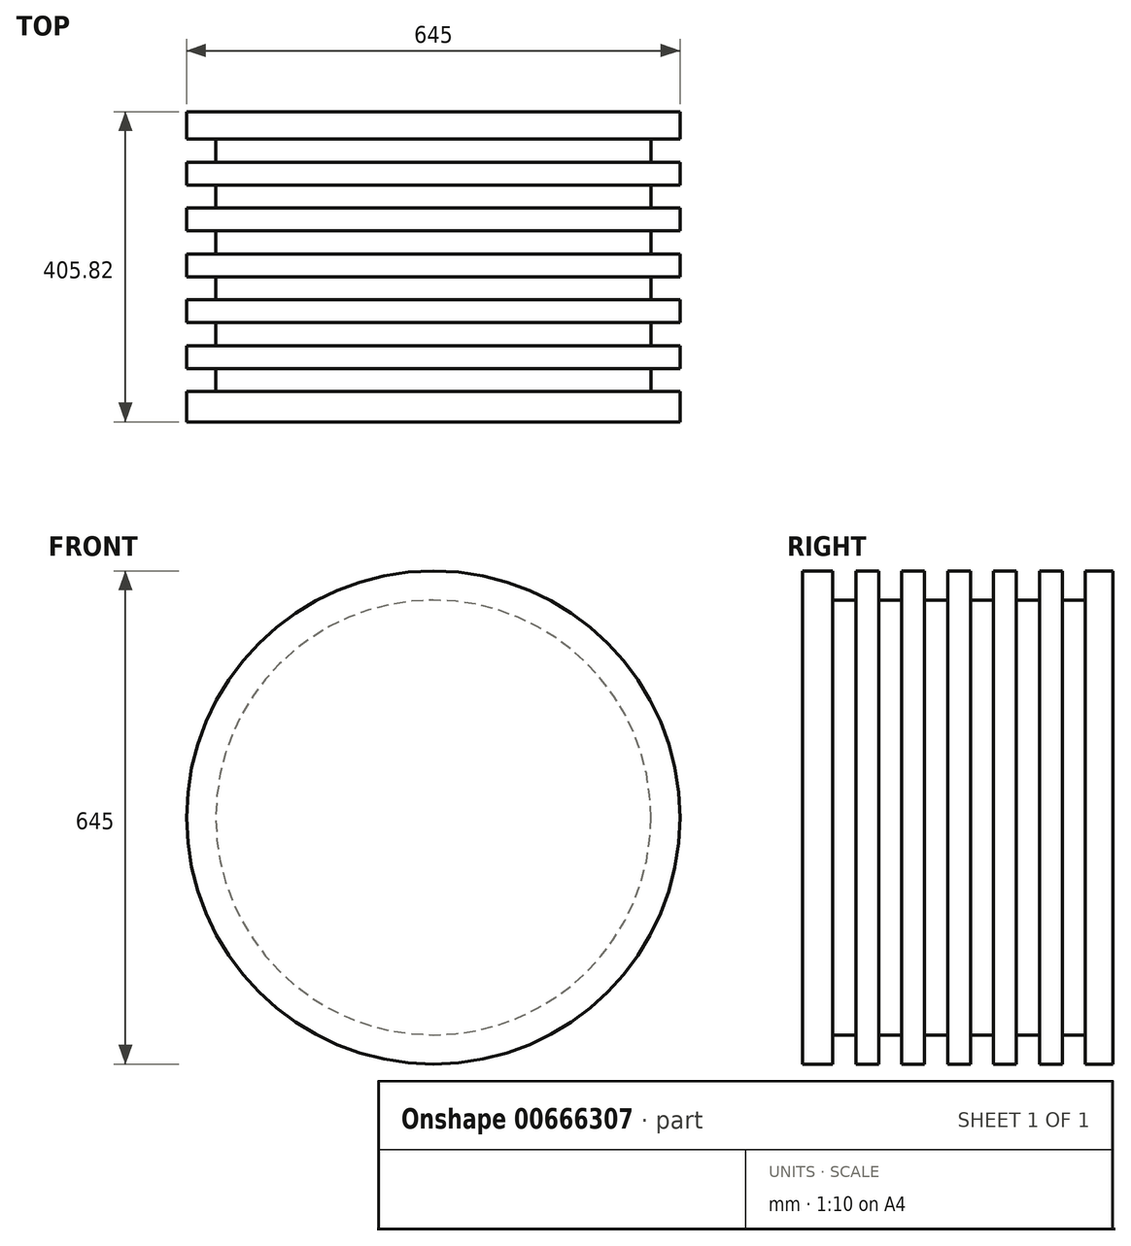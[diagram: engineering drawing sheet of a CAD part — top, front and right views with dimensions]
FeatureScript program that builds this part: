
annotation { "Feature Type Name" : "Feature", "Feature Type Description" : "" }
export const myFeature = defineFeature(function(context is Context, id is Id, definition is map)
    precondition{}
    {
        {
            var Q0;
            Q0=qCreatedBy(makeId("Front.planeOp"),FACE);
            var sketch = newSketch(context, id + "F0", { "sketchPlane" : qUnion([Q0])});
            skCircle(sketch, "E0", {"center": v(0, 0) * mm, "radius": 322.5 * mm});
            skSolve(sketch);
        }
        {
            var Q0;
            Q0=qSketchRegion(id+"F0",true);
            extrude(context, id + "F1", {"entities" : qUnion([Q0]), "depth" : 405.82 * mm});
        }
        {
            var Q0;
            Q0=qCreatedBy(makeId("Right.planeOp"),FACE);
            var sketch = newSketch(context, id + "F2", { "sketchPlane" : qUnion([Q0])});
            skLineSegment(sketch, "E1.bottom", {"start": v(-366.07, 340.51) * mm, "end": v(-336.07, 340.51) * mm});
            skLineSegment(sketch, "E1.top", {"start": v(-366.07, 284.36) * mm, "end": v(-336.07, 284.36) * mm});
            skLineSegment(sketch, "E1.left", {"start": v(-366.07, 340.51) * mm, "end": v(-366.07, 284.36) * mm});
            skLineSegment(sketch, "E1.right", {"start": v(-336.07, 340.51) * mm, "end": v(-336.07, 284.36) * mm});
            skLineSegment(sketch, "E2.1.0.0", {"start": v(-276.07, 340.51) * mm, "end": v(-276.07, 284.36) * mm});
            skLineSegment(sketch, "E2.1.0.1", {"start": v(-306.07, 340.51) * mm, "end": v(-306.07, 284.36) * mm});
            skLineSegment(sketch, "E2.1.0.2", {"start": v(-306.07, 284.36) * mm, "end": v(-276.07, 284.36) * mm});
            skLineSegment(sketch, "E2.1.0.3", {"start": v(-306.07, 340.51) * mm, "end": v(-276.07, 340.51) * mm});
            skLineSegment(sketch, "E2.2.0.0", {"start": v(-216.07, 340.51) * mm, "end": v(-216.07, 284.36) * mm});
            skLineSegment(sketch, "E2.2.0.1", {"start": v(-246.07, 340.51) * mm, "end": v(-246.07, 284.36) * mm});
            skLineSegment(sketch, "E2.2.0.2", {"start": v(-246.07, 284.36) * mm, "end": v(-216.07, 284.36) * mm});
            skLineSegment(sketch, "E2.2.0.3", {"start": v(-246.07, 340.51) * mm, "end": v(-216.07, 340.51) * mm});
            skLineSegment(sketch, "E2.3.0.0", {"start": v(-156.07, 340.51) * mm, "end": v(-156.07, 284.36) * mm});
            skLineSegment(sketch, "E2.3.0.1", {"start": v(-186.07, 340.51) * mm, "end": v(-186.07, 284.36) * mm});
            skLineSegment(sketch, "E2.3.0.2", {"start": v(-186.07, 284.36) * mm, "end": v(-156.07, 284.36) * mm});
            skLineSegment(sketch, "E2.3.0.3", {"start": v(-186.07, 340.51) * mm, "end": v(-156.07, 340.51) * mm});
            skLineSegment(sketch, "E2.4.0.0", {"start": v(-96.07, 340.51) * mm, "end": v(-96.07, 284.36) * mm});
            skLineSegment(sketch, "E2.4.0.1", {"start": v(-126.07, 340.51) * mm, "end": v(-126.07, 284.36) * mm});
            skLineSegment(sketch, "E2.4.0.2", {"start": v(-126.07, 284.36) * mm, "end": v(-96.07, 284.36) * mm});
            skLineSegment(sketch, "E2.4.0.3", {"start": v(-126.07, 340.51) * mm, "end": v(-96.07, 340.51) * mm});
            skLineSegment(sketch, "E2.5.0.0", {"start": v(-36.07, 340.51) * mm, "end": v(-36.07, 284.36) * mm});
            skLineSegment(sketch, "E2.5.0.1", {"start": v(-66.07, 340.51) * mm, "end": v(-66.07, 284.36) * mm});
            skLineSegment(sketch, "E2.5.0.2", {"start": v(-66.07, 284.36) * mm, "end": v(-36.07, 284.36) * mm});
            skLineSegment(sketch, "E2.5.0.3", {"start": v(-66.07, 340.51) * mm, "end": v(-36.07, 340.51) * mm});
            skLineSegment(sketch, "E2.direction1", {"start": v(-366.07, 284.36) * mm, "end": v(-306.07, 284.36) * mm, "construction": true});
            skLineSegment(sketch, "E3", {"start": v(0, 0) * mm, "end": v(-482.61, 0) * mm, "construction": true});
            skSolve(sketch);
        }
        {
            var Q0;
            Q0=makeQuery(id+"F2.imprint","IMPRINT",FACE,{"disambiguationData":[TD([[makeQuery(id+"F2.imprint","IMPRINT",EDGE,{"derivedFrom":sQuery(id+"F2.wireOp",EDGE,"E1.bottom")}),-1.0]])]});
            var Q1;
            Q1=makeQuery(id+"F2.imprint","IMPRINT",FACE,{"disambiguationData":[TD([[makeQuery(id+"F2.imprint","IMPRINT",EDGE,{"derivedFrom":sQuery(id+"F2.wireOp",EDGE,"E2.1.0.0")}),-1.0]])]});
            var Q2;
            Q2=makeQuery(id+"F2.imprint","IMPRINT",FACE,{"disambiguationData":[TD([[makeQuery(id+"F2.imprint","IMPRINT",EDGE,{"derivedFrom":sQuery(id+"F2.wireOp",EDGE,"E2.2.0.0")}),-1.0]])]});
            var Q3;
            Q3=makeQuery(id+"F2.imprint","IMPRINT",FACE,{"disambiguationData":[TD([[makeQuery(id+"F2.imprint","IMPRINT",EDGE,{"derivedFrom":sQuery(id+"F2.wireOp",EDGE,"E2.3.0.0")}),-1.0]])]});
            var Q4;
            Q4=makeQuery(id+"F2.imprint","IMPRINT",FACE,{"disambiguationData":[TD([[makeQuery(id+"F2.imprint","IMPRINT",EDGE,{"derivedFrom":sQuery(id+"F2.wireOp",EDGE,"E2.4.0.0")}),-1.0]])]});
            var Q5;
            Q5=makeQuery(id+"F2.imprint","IMPRINT",FACE,{"disambiguationData":[TD([[makeQuery(id+"F2.imprint","IMPRINT",EDGE,{"derivedFrom":sQuery(id+"F2.wireOp",EDGE,"E2.5.0.0")}),-1.0]])]});
            var Q6;
            Q6=sQuery(id+"F2.wireOp",EDGE,"E2.1.0.3");
            var Q7;
            Q7=sQuery(id+"F2.wireOp",EDGE,"E2.2.0.0");
            var Q8;
            Q8=sQuery(id+"F2.wireOp",EDGE,"E2.2.0.1");
            var Q9;
            Q9=sQuery(id+"F2.wireOp",EDGE,"E2.2.0.2");
            var Q10;
            Q10=sQuery(id+"F2.wireOp",EDGE,"E2.2.0.3");
            var Q11;
            Q11=sQuery(id+"F2.wireOp",EDGE,"E2.3.0.0");
            var Q12;
            Q12=sQuery(id+"F2.wireOp",EDGE,"E2.5.0.3");
            var Q13;
            Q13=sQuery(id+"F2.wireOp",EDGE,"E2.5.0.2");
            var Q14;
            Q14=sQuery(id+"F2.wireOp",EDGE,"E2.5.0.0");
            var Q15;
            Q15=sQuery(id+"F2.wireOp",EDGE,"E2.4.0.2");
            var Q16;
            Q16=sQuery(id+"F2.wireOp",EDGE,"E2.4.0.0");
            var Q17;
            Q17=sQuery(id+"F2.wireOp",EDGE,"E2.5.0.1");
            var Q18;
            Q18=sQuery(id+"F2.wireOp",EDGE,"E2.4.0.3");
            var Q19;
            Q19=sQuery(id+"F2.wireOp",EDGE,"E2.4.0.1");
            var Q20;
            Q20=sQuery(id+"F2.wireOp",EDGE,"E2.3.0.1");
            var Q21;
            Q21=sQuery(id+"F2.wireOp",EDGE,"E2.3.0.2");
            var Q22;
            Q22=sQuery(id+"F2.wireOp",EDGE,"E2.3.0.3");
            var Q23;
            Q23=sQuery(id+"F2.wireOp",EDGE,"E1.bottom");
            var Q24;
            Q24=sQuery(id+"F2.wireOp",EDGE,"E1.left");
            var Q25;
            Q25=sQuery(id+"F2.wireOp",EDGE,"E1.right");
            var Q26;
            Q26=sQuery(id+"F2.wireOp",EDGE,"E2.1.0.0");
            var Q27;
            Q27=sQuery(id+"F2.wireOp",EDGE,"E2.1.0.1");
            var Q28;
            Q28=sQuery(id+"F2.wireOp",EDGE,"E2.1.0.2");
            var Q29;
            Q29=sQuery(id+"F2.wireOp",EDGE,"E1.top");
            var Q30;
            Q30=sQuery(id+"F2.wireOp",EDGE,"E3");
            revolve(context, id + "F3", {"operationType" : NewBodyOperationType.REMOVE, "entities" : qUnion([Q0, Q1, Q2, Q3, Q4, Q5]), "surfaceEntities" : qUnion([Q6, Q7, Q8, Q9, Q10, Q11, Q12, Q13, Q14, Q15, Q16, Q17, Q18, Q19, Q20, Q21, Q22, Q23, Q24, Q25, Q26, Q27, Q28, Q29]), "axis" : qUnion([Q30]), "revolveType" : RevolveType.FULL, "oppositeDirection" : true});
        }
    });
